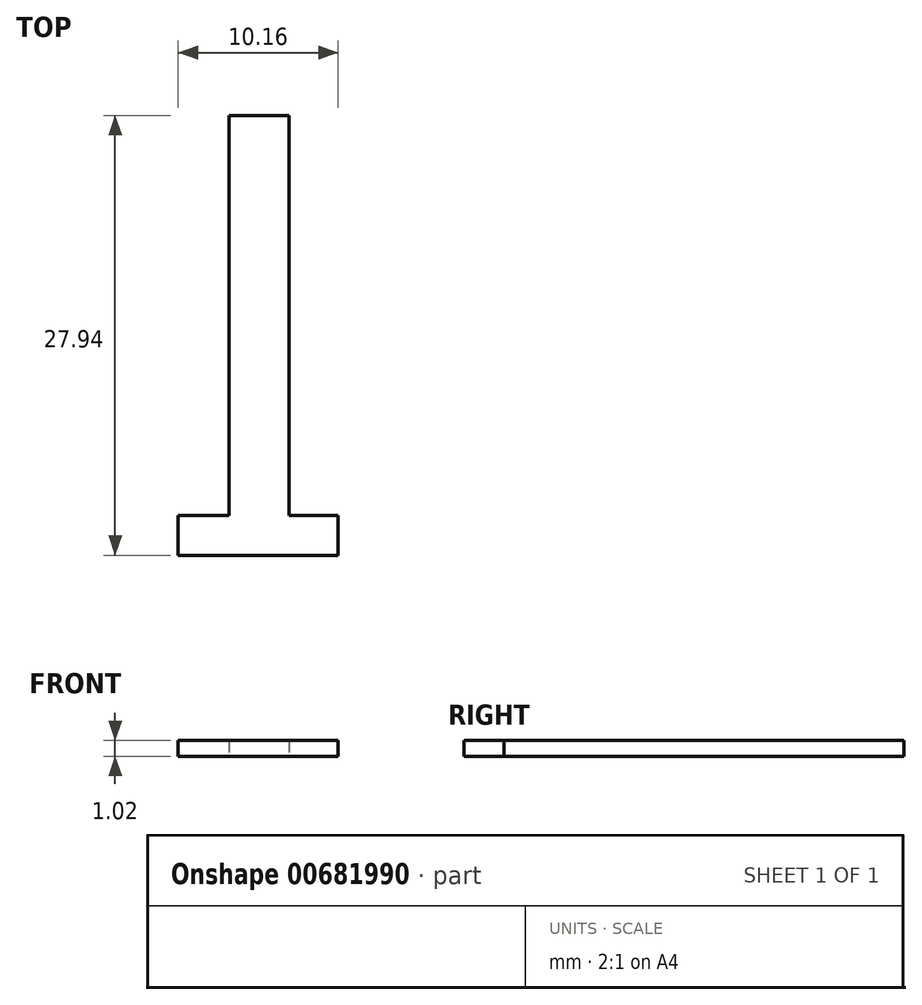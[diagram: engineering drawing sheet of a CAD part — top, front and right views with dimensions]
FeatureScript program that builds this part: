
annotation { "Feature Type Name" : "Feature", "Feature Type Description" : "" }
export const myFeature = defineFeature(function(context is Context, id is Id, definition is map)
    precondition{}
    {
        {
            var Q0;
            Q0=qCreatedBy(makeId("Top.planeOp"),FACE);
            var sketch = newSketch(context, id + "F0", { "sketchPlane" : qUnion([Q0])});
            skLineSegment(sketch, "E0", {"start": v(-33.85, 18.67) * mm, "end": v(-30.04, 18.67) * mm});
            skLineSegment(sketch, "E1", {"start": v(-30.04, 18.67) * mm, "end": v(-30.04, -6.73) * mm});
            skLineSegment(sketch, "E2", {"start": v(-30.04, -6.73) * mm, "end": v(-26.73, -6.73) * mm});
            skLineSegment(sketch, "E3", {"start": v(-26.73, -6.73) * mm, "end": v(-26.73, -9.27) * mm});
            skLineSegment(sketch, "E4", {"start": v(-26.73, -9.27) * mm, "end": v(-37.17, -9.27) * mm});
            skLineSegment(sketch, "E5", {"start": v(-37.17, -9.27) * mm, "end": v(-37.17, -6.73) * mm});
            skLineSegment(sketch, "E6", {"start": v(-37.17, -6.73) * mm, "end": v(-33.86, -6.73) * mm});
            skLineSegment(sketch, "E7", {"start": v(-33.86, -6.73) * mm, "end": v(-33.86, 18.67) * mm});
            skLineSegment(sketch, "E8.bottom", {"start": v(-16.61, -4.19) * mm, "end": v(-12.8, -4.19) * mm});
            skLineSegment(sketch, "E8.top", {"start": v(-16.61, 21.21) * mm, "end": v(-12.8, 21.21) * mm});
            skLineSegment(sketch, "E8.left", {"start": v(-16.61, -4.19) * mm, "end": v(-16.61, 21.21) * mm});
            skLineSegment(sketch, "E8.right", {"start": v(-12.8, -4.19) * mm, "end": v(-12.8, 21.21) * mm});
            skLineSegment(sketch, "E9.bottom", {"start": v(-19.84, -6.73) * mm, "end": v(-9.68, -6.73) * mm});
            skLineSegment(sketch, "E9.top", {"start": v(-19.84, -4.19) * mm, "end": v(-9.68, -4.19) * mm});
            skLineSegment(sketch, "E9.left", {"start": v(-19.84, -6.73) * mm, "end": v(-19.84, -4.19) * mm});
            skLineSegment(sketch, "E9.right", {"start": v(-9.68, -6.73) * mm, "end": v(-9.68, -4.19) * mm});
            skSolve(sketch);
        }
        {
            var Q0;
            Q0=makeQuery(id+"F0.imprint","IMPRINT",FACE,{"disambiguationData":[TD([[makeQuery(id+"F0.imprint","IMPRINT",EDGE,{"derivedFrom":sQuery(id+"F0.wireOp",EDGE,"E8.top")}),-1.0]])]});
            var Q1;
            Q1=makeQuery(id+"F0.imprint","IMPRINT",FACE,{"disambiguationData":[TD([[makeQuery(id+"F0.imprint","IMPRINT",EDGE,{"derivedFrom":sQuery(id+"F0.wireOp",EDGE,"E9.bottom")}),1.0]])]});
            extrude(context, id + "F1", {"entities" : qUnion([Q0, Q1]), "depth" : 1.02 * mm, "offsetDistance" : 25.4 * mm});
        }
    });
